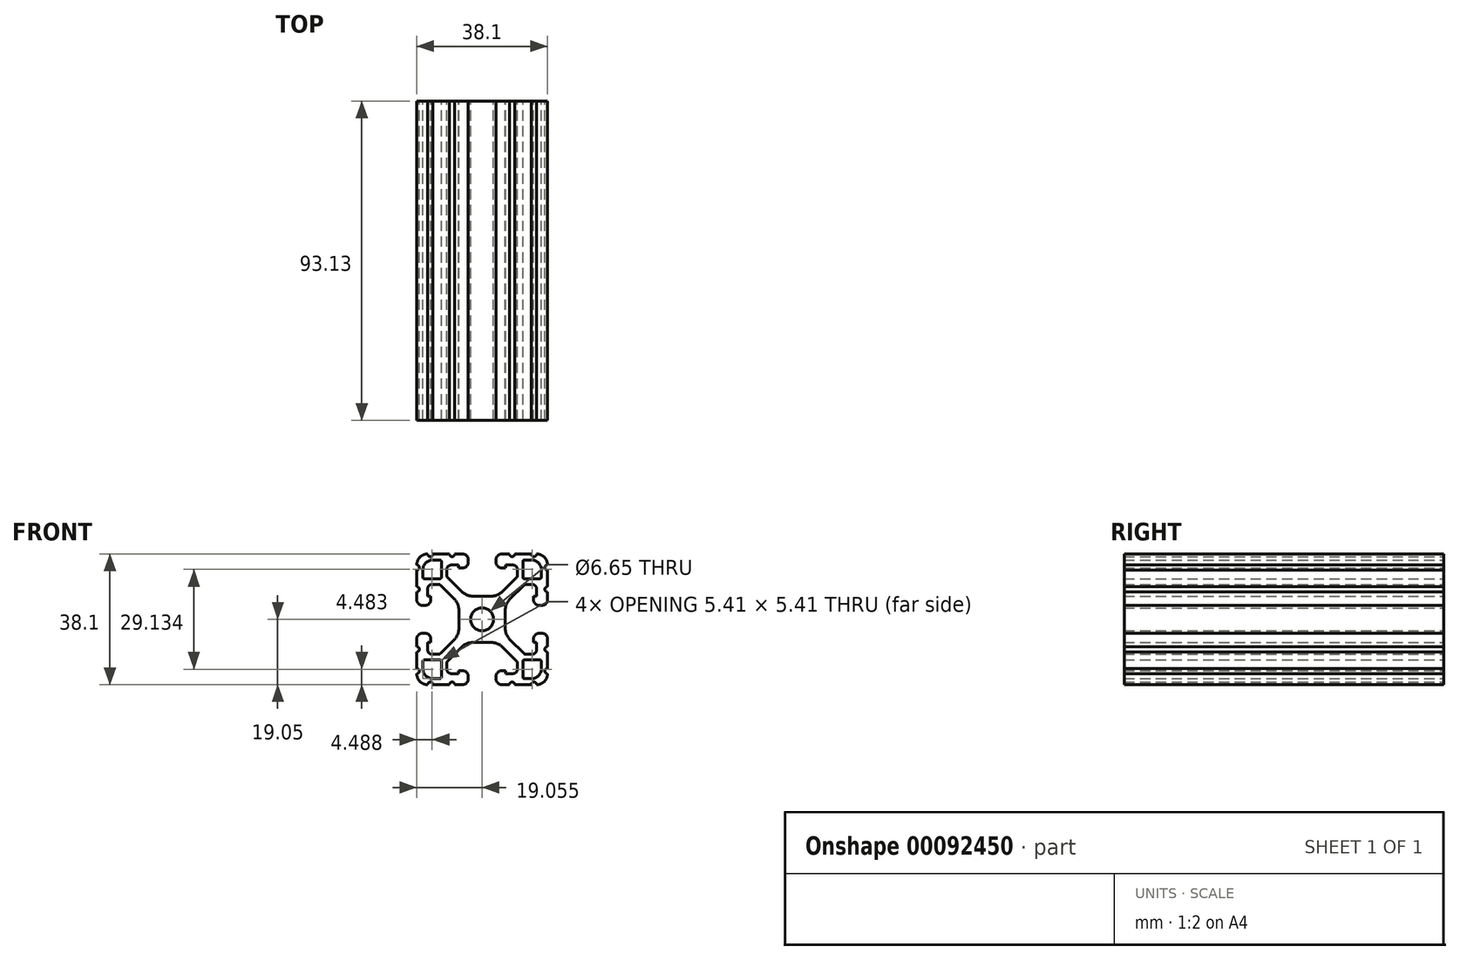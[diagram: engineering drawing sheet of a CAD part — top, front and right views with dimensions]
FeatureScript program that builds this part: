
annotation { "Feature Type Name" : "Feature", "Feature Type Description" : "" }
export const myFeature = defineFeature(function(context is Context, id is Id, definition is map)
    precondition{}
    {
        {
            var Q0;
            Q0=qCreatedBy(makeId("Front.planeOp"),FACE);
            var sketch = newSketch(context, id + "F0", { "sketchPlane" : qUnion([Q0])});
            skLineSegment(sketch, "E0", {"start": v(-110.84, 50.8) * mm, "end": v(-103.85, 50.8) * mm});
            skLineSegment(sketch, "E1", {"start": v(-107.35, 47.3) * mm, "end": v(-107.35, 54.3) * mm});
            skLineSegment(sketch, "E2", {"start": v(-127.2, 42.06) * mm, "end": v(-125.6, 42.06) * mm});
            skLineSegment(sketch, "E3", {"start": v(-126.4, 41.26) * mm, "end": v(-126.4, 42.86) * mm});
            skLineSegment(sketch, "E4", {"start": v(-89.1, 59.54) * mm, "end": v(-87.5, 59.54) * mm});
            skLineSegment(sketch, "E5", {"start": v(-88.3, 58.74) * mm, "end": v(-88.3, 60.34) * mm});
            skLineSegment(sketch, "E6", {"start": v(-89.1, 42.06) * mm, "end": v(-87.5, 42.06) * mm});
            skLineSegment(sketch, "E7", {"start": v(-88.3, 41.26) * mm, "end": v(-88.3, 42.86) * mm});
            skLineSegment(sketch, "E8", {"start": v(-127.2, 59.54) * mm, "end": v(-125.6, 59.54) * mm});
            skLineSegment(sketch, "E9", {"start": v(-126.4, 58.74) * mm, "end": v(-126.4, 60.34) * mm});
            skLineSegment(sketch, "E10", {"start": v(-119.59, 38.94) * mm, "end": v(-124.24, 38.94) * mm});
            skArc(sketch, "E11", {"start": v(-124.24, 38.94) * mm, "mid": v(-124.5, 38.83) * mm, "end": v(-124.62, 38.56) * mm});
            skLineSegment(sketch, "E12", {"start": v(-124.62, 38.56) * mm, "end": v(-124.62, 36.32) * mm});
            skArc(sketch, "E13", {"start": v(-124.62, 36.32) * mm, "mid": v(-123.8, 34.35) * mm, "end": v(-121.82, 33.53) * mm});
            skLineSegment(sketch, "E14", {"start": v(-121.82, 33.53) * mm, "end": v(-119.59, 33.53) * mm});
            skArc(sketch, "E15", {"start": v(-119.59, 33.53) * mm, "mid": v(-119.32, 33.64) * mm, "end": v(-119.2, 33.9) * mm});
            skLineSegment(sketch, "E16", {"start": v(-119.2, 33.9) * mm, "end": v(-119.2, 38.56) * mm});
            skArc(sketch, "E17", {"start": v(-121.82, 68.07) * mm, "mid": v(-123.8, 67.25) * mm, "end": v(-124.62, 65.28) * mm});
            skLineSegment(sketch, "E18", {"start": v(-124.62, 65.28) * mm, "end": v(-124.62, 63.04) * mm});
            skArc(sketch, "E19", {"start": v(-124.62, 63.04) * mm, "mid": v(-124.5, 62.77) * mm, "end": v(-124.24, 62.66) * mm});
            skLineSegment(sketch, "E20", {"start": v(-124.24, 62.66) * mm, "end": v(-119.59, 62.66) * mm});
            skArc(sketch, "E21", {"start": v(-119.59, 62.66) * mm, "mid": v(-119.32, 62.77) * mm, "end": v(-119.2, 63.04) * mm});
            skLineSegment(sketch, "E22", {"start": v(-119.2, 63.04) * mm, "end": v(-119.2, 67.7) * mm});
            skArc(sketch, "E23", {"start": v(-119.2, 67.7) * mm, "mid": v(-119.32, 67.96) * mm, "end": v(-119.59, 68.07) * mm});
            skArc(sketch, "E24", {"start": v(-126.4, 34.94) * mm, "mid": v(-125.63, 35.7) * mm, "end": v(-126.4, 36.47) * mm});
            skLineSegment(sketch, "E25", {"start": v(-126.4, 41.3) * mm, "end": v(-126.4, 36.47) * mm});
            skArc(sketch, "E26", {"start": v(-126.4, 41.3) * mm, "mid": v(-125.63, 42.06) * mm, "end": v(-126.4, 42.82) * mm});
            skLineSegment(sketch, "E27", {"start": v(-126.4, 45.16) * mm, "end": v(-126.4, 42.82) * mm});
            skArc(sketch, "E28", {"start": v(-124.82, 46.74) * mm, "mid": v(-125.93, 46.27) * mm, "end": v(-126.4, 45.16) * mm});
            skLineSegment(sketch, "E29", {"start": v(-123.9, 46.74) * mm, "end": v(-124.82, 46.74) * mm});
            skArc(sketch, "E30", {"start": v(-122.33, 45.16) * mm, "mid": v(-122.8, 46.27) * mm, "end": v(-123.9, 46.74) * mm});
            skLineSegment(sketch, "E31", {"start": v(-122.33, 44.05) * mm, "end": v(-122.33, 45.16) * mm});
            skLineSegment(sketch, "E32", {"start": v(-123.22, 44.05) * mm, "end": v(-122.33, 44.05) * mm});
            skLineSegment(sketch, "E33", {"start": v(-123.22, 41.88) * mm, "end": v(-123.22, 44.05) * mm});
            skArc(sketch, "E34", {"start": v(-123.22, 41.88) * mm, "mid": v(-122.85, 40.98) * mm, "end": v(-121.95, 40.61) * mm});
            skLineSegment(sketch, "E35", {"start": v(-120.09, 40.61) * mm, "end": v(-121.95, 40.61) * mm});
            skArc(sketch, "E36", {"start": v(-120.09, 40.61) * mm, "mid": v(-119.75, 40.68) * mm, "end": v(-119.46, 40.87) * mm});
            skLineSegment(sketch, "E37", {"start": v(-115.5, 44.84) * mm, "end": v(-119.46, 40.87) * mm});
            skArc(sketch, "E38", {"start": v(-115.5, 44.84) * mm, "mid": v(-114.46, 46.38) * mm, "end": v(-114.1, 48.2) * mm});
            skLineSegment(sketch, "E39", {"start": v(-114.1, 53.4) * mm, "end": v(-114.1, 48.2) * mm});
            skArc(sketch, "E40", {"start": v(-114.1, 53.4) * mm, "mid": v(-114.46, 55.22) * mm, "end": v(-115.5, 56.76) * mm});
            skLineSegment(sketch, "E41", {"start": v(-119.46, 60.73) * mm, "end": v(-115.5, 56.76) * mm});
            skArc(sketch, "E42", {"start": v(-119.46, 60.73) * mm, "mid": v(-119.75, 60.92) * mm, "end": v(-120.09, 60.99) * mm});
            skLineSegment(sketch, "E43", {"start": v(-121.95, 60.99) * mm, "end": v(-120.09, 60.99) * mm});
            skArc(sketch, "E44", {"start": v(-121.95, 60.99) * mm, "mid": v(-122.85, 60.62) * mm, "end": v(-123.22, 59.72) * mm});
            skLineSegment(sketch, "E45", {"start": v(-123.22, 57.55) * mm, "end": v(-123.22, 59.72) * mm});
            skLineSegment(sketch, "E46", {"start": v(-122.33, 57.55) * mm, "end": v(-123.22, 57.55) * mm});
            skLineSegment(sketch, "E47", {"start": v(-122.33, 56.44) * mm, "end": v(-122.33, 57.55) * mm});
            skArc(sketch, "E48", {"start": v(-123.9, 54.86) * mm, "mid": v(-122.8, 55.33) * mm, "end": v(-122.33, 56.44) * mm});
            skLineSegment(sketch, "E49", {"start": v(-124.82, 54.86) * mm, "end": v(-123.9, 54.86) * mm});
            skArc(sketch, "E50", {"start": v(-126.4, 56.44) * mm, "mid": v(-125.93, 55.33) * mm, "end": v(-124.82, 54.86) * mm});
            skLineSegment(sketch, "E51", {"start": v(-126.4, 58.78) * mm, "end": v(-126.4, 56.44) * mm});
            skArc(sketch, "E52", {"start": v(-126.4, 58.78) * mm, "mid": v(-125.63, 59.54) * mm, "end": v(-126.4, 60.3) * mm});
            skLineSegment(sketch, "E53", {"start": v(-126.4, 65.13) * mm, "end": v(-126.4, 60.3) * mm});
            skArc(sketch, "E54", {"start": v(-126.4, 65.13) * mm, "mid": v(-125.63, 65.9) * mm, "end": v(-126.4, 66.66) * mm});
            skArc(sketch, "E55", {"start": v(-123.2, 69.85) * mm, "mid": v(-125.47, 68.92) * mm, "end": v(-126.4, 66.66) * mm});
            skArc(sketch, "E56", {"start": v(-123.2, 69.85) * mm, "mid": v(-122.44, 69.09) * mm, "end": v(-121.67, 69.85) * mm});
            skLineSegment(sketch, "E57", {"start": v(-116.84, 69.85) * mm, "end": v(-121.67, 69.85) * mm});
            skArc(sketch, "E58", {"start": v(-116.84, 69.85) * mm, "mid": v(-116.08, 69.09) * mm, "end": v(-115.32, 69.85) * mm});
            skLineSegment(sketch, "E59", {"start": v(-112.98, 69.85) * mm, "end": v(-115.32, 69.85) * mm});
            skArc(sketch, "E60", {"start": v(-111.4, 68.28) * mm, "mid": v(-111.87, 69.39) * mm, "end": v(-112.98, 69.85) * mm});
            skLineSegment(sketch, "E61", {"start": v(-111.4, 67.36) * mm, "end": v(-111.4, 68.28) * mm});
            skArc(sketch, "E62", {"start": v(-112.98, 65.79) * mm, "mid": v(-111.87, 66.25) * mm, "end": v(-111.4, 67.36) * mm});
            skLineSegment(sketch, "E63", {"start": v(-114.16, 65.79) * mm, "end": v(-112.98, 65.79) * mm});
            skLineSegment(sketch, "E64", {"start": v(-114.16, 66.62) * mm, "end": v(-114.16, 65.79) * mm});
            skLineSegment(sketch, "E65", {"start": v(-116.36, 66.62) * mm, "end": v(-114.16, 66.62) * mm});
            skArc(sketch, "E66", {"start": v(-116.36, 66.62) * mm, "mid": v(-117.26, 66.25) * mm, "end": v(-117.63, 65.35) * mm});
            skLineSegment(sketch, "E67", {"start": v(-117.63, 63.58) * mm, "end": v(-117.63, 65.35) * mm});
            skArc(sketch, "E68", {"start": v(-117.63, 63.58) * mm, "mid": v(-117.56, 63.24) * mm, "end": v(-117.37, 62.95) * mm});
            skLineSegment(sketch, "E69", {"start": v(-113.37, 58.95) * mm, "end": v(-117.37, 62.95) * mm});
            skArc(sketch, "E70", {"start": v(-113.37, 58.95) * mm, "mid": v(-111.83, 57.92) * mm, "end": v(-110, 57.56) * mm});
            skLineSegment(sketch, "E71", {"start": v(-104.68, 57.56) * mm, "end": v(-110, 57.56) * mm});
            skArc(sketch, "E72", {"start": v(-104.68, 57.56) * mm, "mid": v(-102.86, 57.92) * mm, "end": v(-101.32, 58.95) * mm});
            skLineSegment(sketch, "E73", {"start": v(-97.32, 62.95) * mm, "end": v(-101.32, 58.95) * mm});
            skArc(sketch, "E74", {"start": v(-97.32, 62.95) * mm, "mid": v(-97.13, 63.24) * mm, "end": v(-97.06, 63.58) * mm});
            skLineSegment(sketch, "E75", {"start": v(-97.06, 65.35) * mm, "end": v(-97.06, 63.58) * mm});
            skArc(sketch, "E76", {"start": v(-97.06, 65.35) * mm, "mid": v(-97.43, 66.25) * mm, "end": v(-98.33, 66.62) * mm});
            skLineSegment(sketch, "E77", {"start": v(-100.53, 66.62) * mm, "end": v(-98.33, 66.62) * mm});
            skLineSegment(sketch, "E78", {"start": v(-100.53, 65.79) * mm, "end": v(-100.53, 66.62) * mm});
            skLineSegment(sketch, "E79", {"start": v(-101.7, 65.79) * mm, "end": v(-100.53, 65.79) * mm});
            skArc(sketch, "E80", {"start": v(-103.28, 67.36) * mm, "mid": v(-102.82, 66.25) * mm, "end": v(-101.7, 65.79) * mm});
            skLineSegment(sketch, "E81", {"start": v(-103.28, 68.28) * mm, "end": v(-103.28, 67.36) * mm});
            skArc(sketch, "E82", {"start": v(-101.7, 69.85) * mm, "mid": v(-102.82, 69.39) * mm, "end": v(-103.28, 68.28) * mm});
            skLineSegment(sketch, "E83", {"start": v(-99.37, 69.85) * mm, "end": v(-101.7, 69.85) * mm});
            skArc(sketch, "E84", {"start": v(-99.37, 69.85) * mm, "mid": v(-98.6, 69.09) * mm, "end": v(-97.85, 69.85) * mm});
            skLineSegment(sketch, "E85", {"start": v(-93.02, 69.85) * mm, "end": v(-97.85, 69.85) * mm});
            skArc(sketch, "E86", {"start": v(-93.02, 69.85) * mm, "mid": v(-92.25, 69.09) * mm, "end": v(-91.48, 69.85) * mm});
            skArc(sketch, "E87", {"start": v(-88.3, 66.66) * mm, "mid": v(-89.23, 68.92) * mm, "end": v(-91.48, 69.85) * mm});
            skArc(sketch, "E88", {"start": v(-88.3, 66.66) * mm, "mid": v(-89.06, 65.9) * mm, "end": v(-88.3, 65.13) * mm});
            skLineSegment(sketch, "E89", {"start": v(-88.3, 60.3) * mm, "end": v(-88.3, 65.13) * mm});
            skArc(sketch, "E90", {"start": v(-88.3, 60.3) * mm, "mid": v(-89.06, 59.54) * mm, "end": v(-88.3, 58.78) * mm});
            skLineSegment(sketch, "E91", {"start": v(-88.3, 56.44) * mm, "end": v(-88.3, 58.78) * mm});
            skArc(sketch, "E92", {"start": v(-89.87, 54.86) * mm, "mid": v(-88.76, 55.33) * mm, "end": v(-88.3, 56.44) * mm});
            skLineSegment(sketch, "E93", {"start": v(-90.78, 54.86) * mm, "end": v(-89.87, 54.86) * mm});
            skArc(sketch, "E94", {"start": v(-92.36, 56.44) * mm, "mid": v(-91.9, 55.33) * mm, "end": v(-90.78, 54.86) * mm});
            skLineSegment(sketch, "E95", {"start": v(-92.36, 57.55) * mm, "end": v(-92.36, 56.44) * mm});
            skLineSegment(sketch, "E96", {"start": v(-91.47, 57.55) * mm, "end": v(-92.36, 57.55) * mm});
            skLineSegment(sketch, "E97", {"start": v(-91.47, 59.72) * mm, "end": v(-91.47, 57.55) * mm});
            skArc(sketch, "E98", {"start": v(-91.47, 59.72) * mm, "mid": v(-91.84, 60.62) * mm, "end": v(-92.74, 60.99) * mm});
            skLineSegment(sketch, "E99", {"start": v(-94.6, 60.99) * mm, "end": v(-92.74, 60.99) * mm});
            skArc(sketch, "E100", {"start": v(-94.6, 60.99) * mm, "mid": v(-94.94, 60.92) * mm, "end": v(-95.23, 60.73) * mm});
            skLineSegment(sketch, "E101", {"start": v(-99.2, 56.76) * mm, "end": v(-95.23, 60.73) * mm});
            skArc(sketch, "E102", {"start": v(-99.2, 56.76) * mm, "mid": v(-100.23, 55.22) * mm, "end": v(-100.59, 53.4) * mm});
            skLineSegment(sketch, "E103", {"start": v(-100.59, 48.2) * mm, "end": v(-100.59, 53.4) * mm});
            skArc(sketch, "E104", {"start": v(-100.59, 48.2) * mm, "mid": v(-100.23, 46.38) * mm, "end": v(-99.2, 44.84) * mm});
            skLineSegment(sketch, "E105", {"start": v(-95.23, 40.87) * mm, "end": v(-99.2, 44.84) * mm});
            skArc(sketch, "E106", {"start": v(-95.23, 40.87) * mm, "mid": v(-94.94, 40.68) * mm, "end": v(-94.6, 40.61) * mm});
            skLineSegment(sketch, "E107", {"start": v(-92.74, 40.61) * mm, "end": v(-94.6, 40.61) * mm});
            skArc(sketch, "E108", {"start": v(-92.74, 40.61) * mm, "mid": v(-91.84, 40.98) * mm, "end": v(-91.47, 41.88) * mm});
            skLineSegment(sketch, "E109", {"start": v(-91.47, 44.05) * mm, "end": v(-91.47, 41.88) * mm});
            skLineSegment(sketch, "E110", {"start": v(-92.36, 44.05) * mm, "end": v(-91.47, 44.05) * mm});
            skLineSegment(sketch, "E111", {"start": v(-92.36, 45.16) * mm, "end": v(-92.36, 44.05) * mm});
            skArc(sketch, "E112", {"start": v(-90.78, 46.74) * mm, "mid": v(-91.9, 46.27) * mm, "end": v(-92.36, 45.16) * mm});
            skLineSegment(sketch, "E113", {"start": v(-89.87, 46.74) * mm, "end": v(-90.78, 46.74) * mm});
            skArc(sketch, "E114", {"start": v(-88.3, 45.16) * mm, "mid": v(-88.76, 46.27) * mm, "end": v(-89.87, 46.74) * mm});
            skLineSegment(sketch, "E115", {"start": v(-88.3, 42.82) * mm, "end": v(-88.3, 45.16) * mm});
            skArc(sketch, "E116", {"start": v(-88.3, 42.82) * mm, "mid": v(-89.06, 42.06) * mm, "end": v(-88.3, 41.3) * mm});
            skLineSegment(sketch, "E117", {"start": v(-88.3, 36.47) * mm, "end": v(-88.3, 41.3) * mm});
            skArc(sketch, "E118", {"start": v(-88.3, 36.47) * mm, "mid": v(-89.06, 35.7) * mm, "end": v(-88.3, 34.94) * mm});
            skArc(sketch, "E119", {"start": v(-91.48, 31.75) * mm, "mid": v(-89.23, 32.68) * mm, "end": v(-88.3, 34.94) * mm});
            skArc(sketch, "E120", {"start": v(-91.48, 31.75) * mm, "mid": v(-92.25, 32.51) * mm, "end": v(-93.02, 31.75) * mm});
            skLineSegment(sketch, "E121", {"start": v(-97.85, 31.75) * mm, "end": v(-93.02, 31.75) * mm});
            skArc(sketch, "E122", {"start": v(-97.85, 31.75) * mm, "mid": v(-98.6, 32.51) * mm, "end": v(-99.37, 31.75) * mm});
            skLineSegment(sketch, "E123", {"start": v(-101.7, 31.75) * mm, "end": v(-99.37, 31.75) * mm});
            skArc(sketch, "E124", {"start": v(-103.28, 33.32) * mm, "mid": v(-102.82, 32.21) * mm, "end": v(-101.7, 31.75) * mm});
            skLineSegment(sketch, "E125", {"start": v(-103.28, 34.24) * mm, "end": v(-103.28, 33.32) * mm});
            skArc(sketch, "E126", {"start": v(-101.7, 35.81) * mm, "mid": v(-102.82, 35.35) * mm, "end": v(-103.28, 34.24) * mm});
            skLineSegment(sketch, "E127", {"start": v(-100.53, 35.81) * mm, "end": v(-101.7, 35.81) * mm});
            skLineSegment(sketch, "E128", {"start": v(-100.53, 34.98) * mm, "end": v(-100.53, 35.81) * mm});
            skLineSegment(sketch, "E129", {"start": v(-98.33, 34.98) * mm, "end": v(-100.53, 34.98) * mm});
            skArc(sketch, "E130", {"start": v(-98.33, 34.98) * mm, "mid": v(-97.43, 35.35) * mm, "end": v(-97.06, 36.25) * mm});
            skLineSegment(sketch, "E131", {"start": v(-97.06, 38.02) * mm, "end": v(-97.06, 36.25) * mm});
            skArc(sketch, "E132", {"start": v(-97.06, 38.02) * mm, "mid": v(-97.13, 38.36) * mm, "end": v(-97.32, 38.65) * mm});
            skLineSegment(sketch, "E133", {"start": v(-101.32, 42.65) * mm, "end": v(-97.32, 38.65) * mm});
            skArc(sketch, "E134", {"start": v(-101.32, 42.65) * mm, "mid": v(-102.86, 43.68) * mm, "end": v(-104.68, 44.04) * mm});
            skLineSegment(sketch, "E135", {"start": v(-110, 44.04) * mm, "end": v(-104.68, 44.04) * mm});
            skArc(sketch, "E136", {"start": v(-110, 44.04) * mm, "mid": v(-111.83, 43.68) * mm, "end": v(-113.37, 42.65) * mm});
            skLineSegment(sketch, "E137", {"start": v(-117.37, 38.65) * mm, "end": v(-113.37, 42.65) * mm});
            skArc(sketch, "E138", {"start": v(-117.37, 38.65) * mm, "mid": v(-117.56, 38.36) * mm, "end": v(-117.63, 38.02) * mm});
            skLineSegment(sketch, "E139", {"start": v(-117.63, 36.25) * mm, "end": v(-117.63, 38.02) * mm});
            skArc(sketch, "E140", {"start": v(-117.63, 36.25) * mm, "mid": v(-117.26, 35.35) * mm, "end": v(-116.36, 34.98) * mm});
            skLineSegment(sketch, "E141", {"start": v(-114.16, 34.98) * mm, "end": v(-116.36, 34.98) * mm});
            skLineSegment(sketch, "E142", {"start": v(-114.16, 35.81) * mm, "end": v(-114.16, 34.98) * mm});
            skLineSegment(sketch, "E143", {"start": v(-112.98, 35.81) * mm, "end": v(-114.16, 35.81) * mm});
            skArc(sketch, "E144", {"start": v(-111.4, 34.24) * mm, "mid": v(-111.87, 35.35) * mm, "end": v(-112.98, 35.81) * mm});
            skLineSegment(sketch, "E145", {"start": v(-111.4, 33.32) * mm, "end": v(-111.4, 34.24) * mm});
            skArc(sketch, "E146", {"start": v(-112.98, 31.75) * mm, "mid": v(-111.87, 32.21) * mm, "end": v(-111.4, 33.32) * mm});
            skLineSegment(sketch, "E147", {"start": v(-115.32, 31.75) * mm, "end": v(-112.98, 31.75) * mm});
            skArc(sketch, "E148", {"start": v(-115.32, 31.75) * mm, "mid": v(-116.08, 32.51) * mm, "end": v(-116.84, 31.75) * mm});
            skLineSegment(sketch, "E149", {"start": v(-121.67, 31.75) * mm, "end": v(-116.84, 31.75) * mm});
            skArc(sketch, "E150", {"start": v(-121.67, 31.75) * mm, "mid": v(-122.44, 32.51) * mm, "end": v(-123.2, 31.75) * mm});
            skLineSegment(sketch, "E151", {"start": v(-90.45, 38.94) * mm, "end": v(-95.1, 38.94) * mm});
            skArc(sketch, "E152", {"start": v(-95.1, 38.94) * mm, "mid": v(-95.37, 38.83) * mm, "end": v(-95.48, 38.56) * mm});
            skLineSegment(sketch, "E153", {"start": v(-95.48, 38.56) * mm, "end": v(-95.48, 33.9) * mm});
            skArc(sketch, "E154", {"start": v(-95.48, 33.9) * mm, "mid": v(-95.37, 33.64) * mm, "end": v(-95.1, 33.53) * mm});
            skLineSegment(sketch, "E155", {"start": v(-95.1, 33.53) * mm, "end": v(-92.87, 33.53) * mm});
            skArc(sketch, "E156", {"start": v(-92.87, 33.53) * mm, "mid": v(-90.9, 34.35) * mm, "end": v(-90.07, 36.32) * mm});
            skLineSegment(sketch, "E157", {"start": v(-90.07, 36.32) * mm, "end": v(-90.07, 38.56) * mm});
            skArc(sketch, "E158", {"start": v(-95.1, 68.07) * mm, "mid": v(-95.37, 67.96) * mm, "end": v(-95.48, 67.7) * mm});
            skLineSegment(sketch, "E159", {"start": v(-95.48, 67.7) * mm, "end": v(-95.48, 63.04) * mm});
            skArc(sketch, "E160", {"start": v(-95.48, 63.04) * mm, "mid": v(-95.37, 62.77) * mm, "end": v(-95.1, 62.66) * mm});
            skLineSegment(sketch, "E161", {"start": v(-95.1, 62.66) * mm, "end": v(-90.45, 62.66) * mm});
            skArc(sketch, "E162", {"start": v(-90.45, 62.66) * mm, "mid": v(-90.18, 62.77) * mm, "end": v(-90.07, 63.04) * mm});
            skLineSegment(sketch, "E163", {"start": v(-90.07, 63.04) * mm, "end": v(-90.07, 65.28) * mm});
            skArc(sketch, "E164", {"start": v(-90.07, 65.28) * mm, "mid": v(-90.9, 67.25) * mm, "end": v(-92.87, 68.07) * mm});
            skLineSegment(sketch, "E165", {"start": v(-119.59, 68.07) * mm, "end": v(-121.82, 68.07) * mm});
            skCircle(sketch, "E166", {"center": v(-107.35, 50.8) * mm, "radius": 3.33 * mm});
            skArc(sketch, "E167", {"start": v(-126.4, 34.94) * mm, "mid": v(-125.47, 32.68) * mm, "end": v(-123.2, 31.75) * mm});
            skArc(sketch, "E168", {"start": v(-90.07, 38.56) * mm, "mid": v(-90.18, 38.83) * mm, "end": v(-90.45, 38.94) * mm});
            skLineSegment(sketch, "E169", {"start": v(-92.87, 68.07) * mm, "end": v(-95.1, 68.07) * mm});
            skArc(sketch, "E170", {"start": v(-119.2, 38.56) * mm, "mid": v(-119.32, 38.83) * mm, "end": v(-119.59, 38.94) * mm});
            skSolve(sketch);
        }
        {
            var Q0;
            Q0=makeQuery(id+"F0.imprint","IMPRINT",FACE,{"disambiguationData":[TD([[makeQuery(id+"F0.imprint","IMPRINT",EDGE,{"derivedFrom":sQuery(id+"F0.wireOp",EDGE,"E10")}),-1.0]])]});
            extrude(context, id + "F1", {"entities" : qUnion([Q0]), "depth" : 93.13 * mm});
        }
    });
